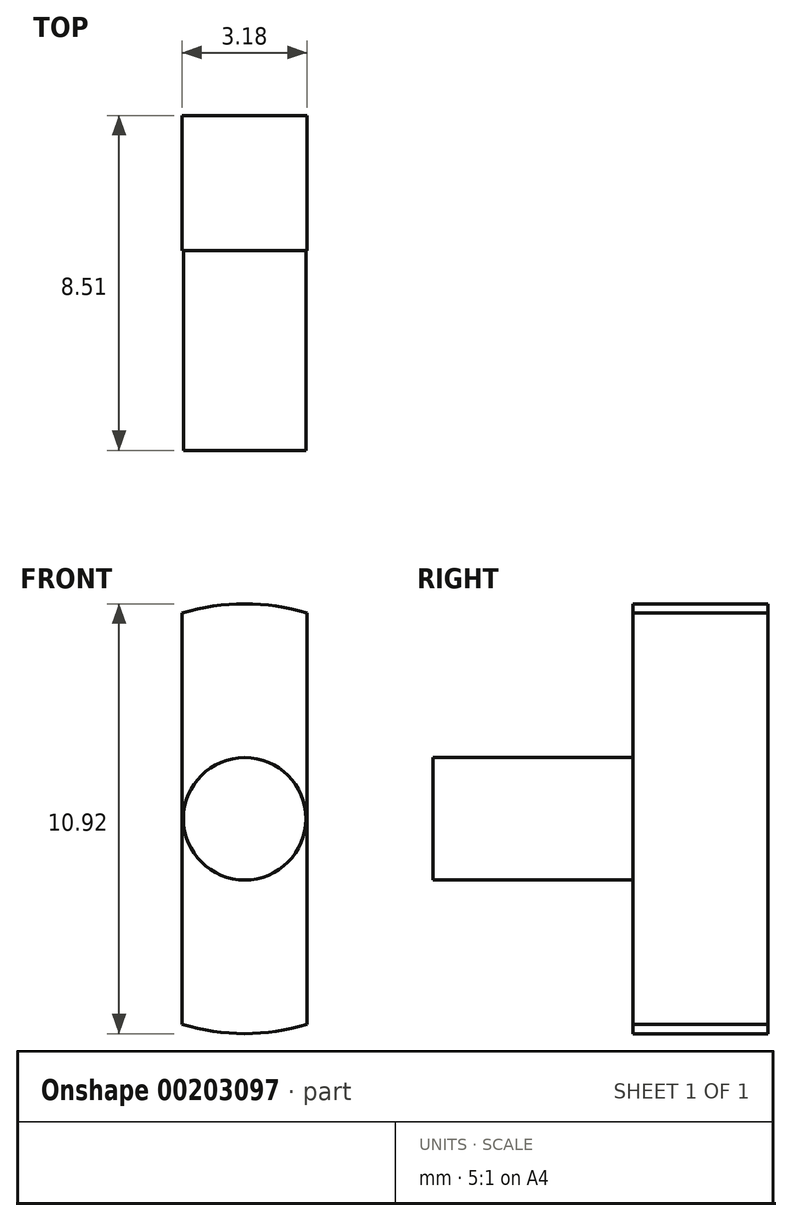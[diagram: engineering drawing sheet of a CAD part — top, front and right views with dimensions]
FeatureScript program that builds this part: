
annotation { "Feature Type Name" : "Feature", "Feature Type Description" : "" }
export const myFeature = defineFeature(function(context is Context, id is Id, definition is map)
    precondition{}
    {
        {
            var Q0;
            Q0=qCreatedBy(makeId("Front.planeOp"),FACE);
            var sketch = newSketch(context, id + "F0", { "sketchPlane" : qUnion([Q0])});
            skArc(sketch, "E0", {"start": v(1.59, 5.23) * mm, "mid": v(0, 5.46) * mm, "end": v(-1.59, 5.23) * mm});
            skLineSegment(sketch, "E1", {"start": v(-1.59, 5.23) * mm, "end": v(-1.59, -5.23) * mm});
            skLineSegment(sketch, "E2.MirrorCS", {"start": v(1.59, 5.23) * mm, "end": v(1.59, -5.23) * mm});
            skPoint(sketch, "E3.orphan", {"position": v(-1.59, 7.38) * mm});
            skPoint(sketch, "E4.orphan", {"position": v(1.59, 7.38) * mm});
            skPoint(sketch, "E5.orphan", {"position": v(-1.59, -7.74) * mm});
            skPoint(sketch, "E6.orphan", {"position": v(1.59, -7.74) * mm});
            skArc(sketch, "E7.trimOffspring", {"start": v(-1.59, -5.23) * mm, "mid": v(0, -5.46) * mm, "end": v(1.59, -5.23) * mm});
            skSolve(sketch);
        }
        {
            var Q0;
            Q0 = qSketchRegion(id + "F0", true);
            extrude(context, id + "F1", {"entities" : qUnion([Q0]), "oppositeDirection" : true, "depth" : 3.43 * mm});
        }
        {
            var Q0;
            Q0=makeQuery(id+"F1.opExtrude","CAP_FACE",FACE,{"disambiguationData":[OSD([sQuery(id+"F0.wireOp",EDGE,"E0"),sQuery(id+"F0.wireOp",EDGE,"E1"),sQuery(id+"F0.wireOp",EDGE,"E2.MirrorCS"),sQuery(id+"F0.wireOp",EDGE,"E7.trimOffspring")])],"isStart":true});
            var sketch = newSketch(context, id + "F2", { "sketchPlane" : qUnion([Q0])});
            skCircle(sketch, "E8", {"center": v(0, 0) * mm, "radius": 1.56 * mm});
            skSolve(sketch);
        }
        {
            var Q0;
            Q0 = qSketchRegion(id + "F2", true);
            extrude(context, id + "F3", {"entities" : qUnion([Q0]), "operationType" : NewBodyOperationType.ADD, "depth" : 5.08 * mm});
        }
    });
